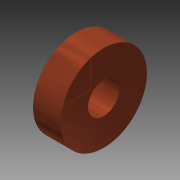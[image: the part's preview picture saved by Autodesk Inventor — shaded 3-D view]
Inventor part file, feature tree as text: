
AUTODESK INVENTOR PART (.ipt)
format: ipt  version: 2015 (Build 190159000, 159)  size: 101,376 bytes
history: native  units: mm
features: extrude x1, sketch x1
ambient origin geometry x8: Origin, YZ Plane, XZ Plane, XY Plane, X Axis, Y Axis, Z Axis, Center Point
bodies: Solid1 (feature_tree)
feature tree (2):
  extrude  "Extrusion1"  Depth=7.0mm
  sketch  "Sketch1"  dims[d0=8.0mm d1=22.0mm d2=7.0mm d3=0.0mm]
